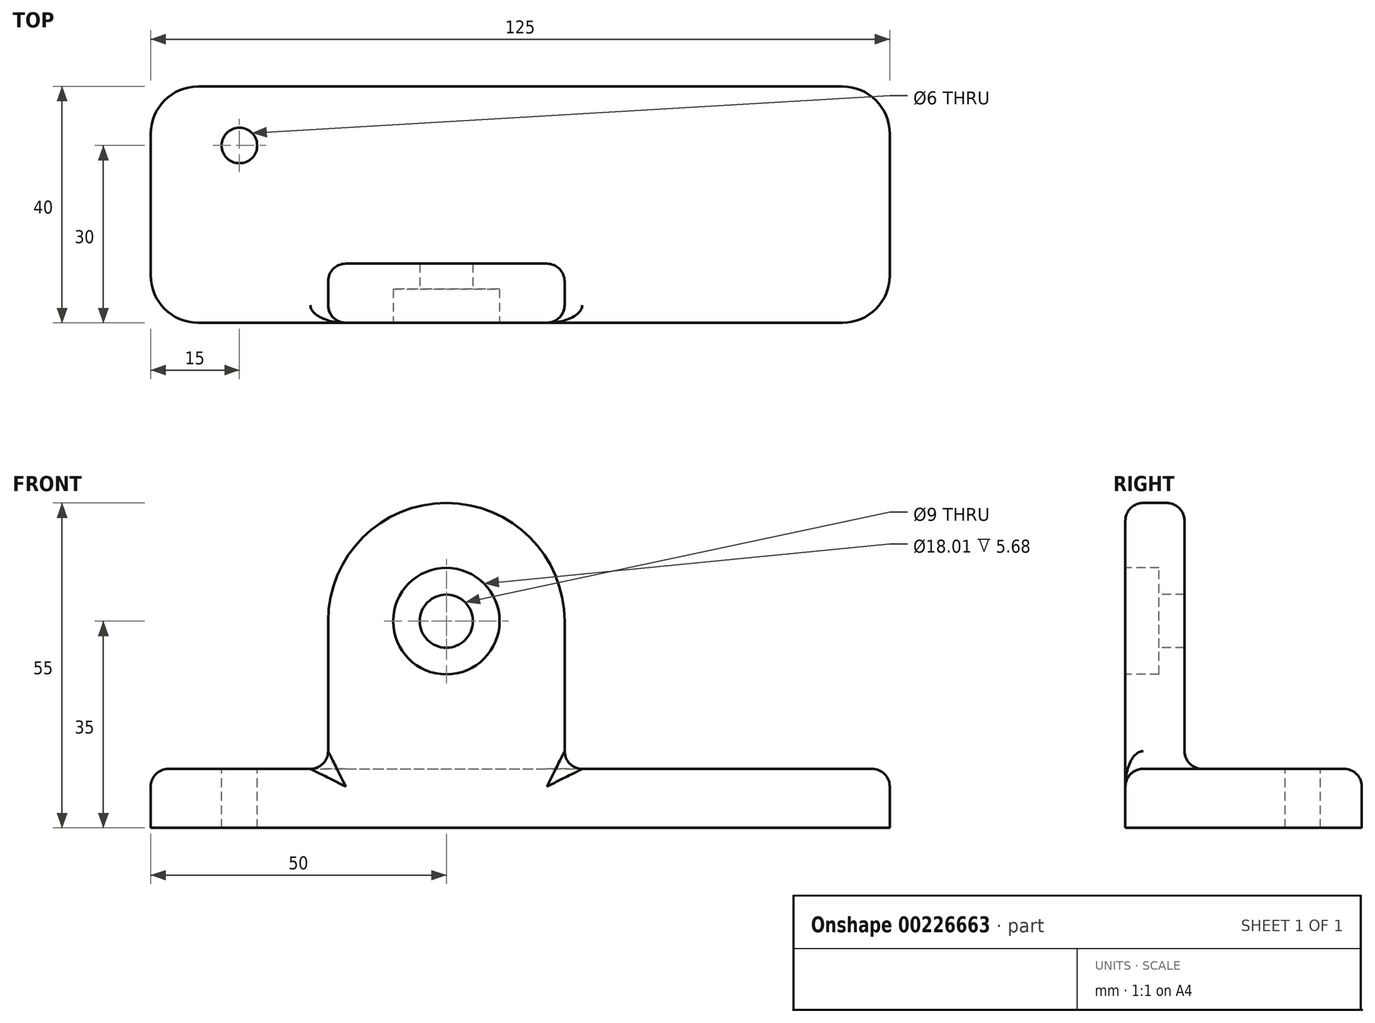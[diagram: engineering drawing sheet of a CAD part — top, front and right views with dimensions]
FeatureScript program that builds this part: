
annotation { "Feature Type Name" : "Feature", "Feature Type Description" : "" }
export const myFeature = defineFeature(function(context is Context, id is Id, definition is map)
    precondition{}
    {
        {
            var Q0;
            Q0=qCreatedBy(makeId("Top.planeOp"),FACE);
            var sketch = newSketch(context, id + "F0", { "sketchPlane" : qUnion([Q0])});
            skLineSegment(sketch, "E0.bottom", {"start": v(-62.5, 20) * mm, "end": v(62.5, 20) * mm});
            skLineSegment(sketch, "E0.top", {"start": v(-62.5, -20) * mm, "end": v(62.5, -20) * mm});
            skLineSegment(sketch, "E0.left", {"start": v(-62.5, 20) * mm, "end": v(-62.5, -20) * mm});
            skLineSegment(sketch, "E0.right", {"start": v(62.5, 20) * mm, "end": v(62.5, -20) * mm});
            skPoint(sketch, "E0.middle", {"position": v(0, 0) * mm});
            skSolve(sketch);
        }
        {
            var Q0;
            Q0 = qSketchRegion(id + "F0", true);
            extrude(context, id + "F1", {"entities" : qUnion([Q0]), "depth" : 10 * mm});
        }
        {
            var Q0;
            Q0=makeQuery(id+"F1.opExtrude","CAP_FACE",FACE,{"disambiguationData":[OSD([sQuery(id+"F0.wireOp",EDGE,"E0.bottom"),sQuery(id+"F0.wireOp",EDGE,"E0.top"),sQuery(id+"F0.wireOp",EDGE,"E0.left"),sQuery(id+"F0.wireOp",EDGE,"E0.right")])],"isStart":false});
            var sketch = newSketch(context, id + "F2", { "sketchPlane" : qUnion([Q0])});
            skLineSegment(sketch, "E1.bottom", {"start": v(-32.5, -20) * mm, "end": v(7.5, -20) * mm});
            skLineSegment(sketch, "E1.top", {"start": v(-32.5, -10) * mm, "end": v(7.5, -10) * mm});
            skLineSegment(sketch, "E1.left", {"start": v(-32.5, -20) * mm, "end": v(-32.5, -10) * mm});
            skLineSegment(sketch, "E1.right", {"start": v(7.5, -20) * mm, "end": v(7.5, -10) * mm});
            skSolve(sketch);
        }
        {
            var Q0;
            Q0 = qSketchRegion(id + "F2", true);
            extrude(context, id + "F3", {"entities" : qUnion([Q0]), "operationType" : NewBodyOperationType.ADD, "depth" : 25 * mm});
        }
        {
            var Q0;
            Q0=makeQuery(id+"F3.boolean.opBoolean","MERGE",FACE,{"derivedFrom":[makeQuery(id+"F1.opExtrude","SWEPT_FACE",FACE,{"disambiguationData":[OSD([sQuery(id+"F0.wireOp",EDGE,"E0.top")])]}),makeQuery(id+"F3.opExtrude","SWEPT_FACE",FACE,{"disambiguationData":[OSD([sQuery(id+"F2.wireOp",EDGE,"E1.bottom")])]})]});
            var sketch = newSketch(context, id + "F4", { "sketchPlane" : qUnion([Q0])});
            skCircle(sketch, "E2", {"center": v(-12.5, 35) * mm, "radius": 20 * mm});
            skSolve(sketch);
        }
        {
            var Q0;
            Q0 = qSketchRegion(id + "F4", true);
            extrude(context, id + "F5", {"entities" : qUnion([Q0]), "operationType" : NewBodyOperationType.ADD, "oppositeDirection" : true, "depth" : 10 * mm});
        }
        {
            var Q0;
            Q0=makeQuery(id+"F1.opExtrude","CAP_FACE",FACE,{"disambiguationData":[OSD([sQuery(id+"F0.wireOp",EDGE,"E0.bottom"),sQuery(id+"F0.wireOp",EDGE,"E0.top"),sQuery(id+"F0.wireOp",EDGE,"E0.left"),sQuery(id+"F0.wireOp",EDGE,"E0.right")])],"isStart":false});
            var sketch = newSketch(context, id + "F6", { "sketchPlane" : qUnion([Q0])});
            skCircle(sketch, "E3", {"center": v(-47.5, 10) * mm, "radius": 3 * mm});
            skSolve(sketch);
        }
        {
            var Q0;
            Q0=makeQuery(id+"F5.boolean.opBoolean","MERGE",FACE,{"derivedFrom":[makeQuery(id+"F3.boolean.opBoolean","MERGE",FACE,{"derivedFrom":[makeQuery(id+"F1.opExtrude","SWEPT_FACE",FACE,{"disambiguationData":[OSD([sQuery(id+"F0.wireOp",EDGE,"E0.top")])]}),makeQuery(id+"F3.opExtrude","SWEPT_FACE",FACE,{"disambiguationData":[OSD([sQuery(id+"F2.wireOp",EDGE,"E1.bottom")])]})]}),makeQuery(id+"F5.opExtrude","CAP_FACE",FACE,{"disambiguationData":[OSD([sQuery(id+"F4.wireOp",EDGE,"E2")])],"isStart":true})]});
            var sketch = newSketch(context, id + "F7", { "sketchPlane" : qUnion([Q0])});
            skCircle(sketch, "E4", {"center": v(-12.5, 35) * mm, "radius": 4.5 * mm});
            skSolve(sketch);
        }
        {
            var Q0;
            Q0 = qSketchRegion(id + "F7", true);
            extrude(context, id + "F8", {"entities" : qUnion([Q0]), "operationType" : NewBodyOperationType.REMOVE, "oppositeDirection" : true, "depth" : 25 * mm});
        }
        {
            var Q0;
            Q0=makeQuery(id+"F5.boolean.opBoolean","MERGE",FACE,{"derivedFrom":[makeQuery(id+"F3.boolean.opBoolean","MERGE",FACE,{"derivedFrom":[makeQuery(id+"F1.opExtrude","SWEPT_FACE",FACE,{"disambiguationData":[OSD([sQuery(id+"F0.wireOp",EDGE,"E0.top")])]}),makeQuery(id+"F3.opExtrude","SWEPT_FACE",FACE,{"disambiguationData":[OSD([sQuery(id+"F2.wireOp",EDGE,"E1.bottom")])]})]}),makeQuery(id+"F5.opExtrude","CAP_FACE",FACE,{"disambiguationData":[OSD([sQuery(id+"F4.wireOp",EDGE,"E2")])],"isStart":true})]});
            var sketch = newSketch(context, id + "F9", { "sketchPlane" : qUnion([Q0])});
            skCircle(sketch, "E5", {"center": v(-12.5, 35) * mm, "radius": 9 * mm});
            skSolve(sketch);
        }
        {
            var Q0;
            Q0 = qSketchRegion(id + "F9", true);
            extrude(context, id + "F10", {"entities" : qUnion([Q0]), "operationType" : NewBodyOperationType.REMOVE, "oppositeDirection" : true, "depth" : 5.68 * mm});
        }
        {
            var Q0;
            Q0=makeQuery(id+"F1.opExtrude","SWEPT_EDGE",EDGE,{"disambiguationData":[OSD([sQuery(id+"F0.wireOp",EDGE,"E0.top"),sQuery(id+"F0.wireOp",EDGE,"E0.right")])]});
            var Q1;
            Q1=makeQuery(id+"F1.opExtrude","SWEPT_EDGE",EDGE,{"disambiguationData":[OSD([sQuery(id+"F0.wireOp",EDGE,"E0.bottom"),sQuery(id+"F0.wireOp",EDGE,"E0.right")])]});
            var Q2;
            Q2=makeQuery(id+"F1.opExtrude","SWEPT_EDGE",EDGE,{"disambiguationData":[OSD([sQuery(id+"F0.wireOp",EDGE,"E0.top"),sQuery(id+"F0.wireOp",EDGE,"E0.left")])]});
            var Q3;
            Q3=makeQuery(id+"F1.opExtrude","SWEPT_EDGE",EDGE,{"disambiguationData":[OSD([sQuery(id+"F0.wireOp",EDGE,"E0.bottom"),sQuery(id+"F0.wireOp",EDGE,"E0.left")])]});
            fillet(context, id + "F11", {"entities" : qUnion([Q0, Q1, Q2, Q3]), "radius" : 8 * mm, "tangentPropagation" : true, "allowEdgeOverflow" : false});
        }
        {
            var Q0;
            {var subQ0=sQuery(id+"F0.wireOp",EDGE,"E0.right");var subQ1=sQuery(id+"F0.wireOp",EDGE,"E0.top");Q0=makeQuery(id+"F3.boolean.opBoolean","SPLIT",EDGE,{"disambiguationData":[TD([makeQuery(id+"F1.opExtrude","SWEPT_FACE",FACE,{"disambiguationData":[OSD([subQ0])]})])],"derivedFrom":makeQuery(id+"F1.opExtrude","CAP_EDGE",EDGE,{"disambiguationData":[OSD([subQ1])],"isStart":false})});}
            var Q1;
            Q1=makeQuery(id+"F3.opExtrude","SWEPT_EDGE",EDGE,{"disambiguationData":[OSD([sQuery(id+"F0.wireOp",EDGE,"E0.top"),sQuery(id+"F2.wireOp",EDGE,"E1.bottom"),sQuery(id+"F2.wireOp",EDGE,"E1.right")])]});
            var Q2;
            Q2=makeQuery(id+"F3.opExtrude","SWEPT_EDGE",EDGE,{"disambiguationData":[OSD([sQuery(id+"F2.wireOp",EDGE,"E1.top"),sQuery(id+"F2.wireOp",EDGE,"E1.right")])]});
            fillet(context, id + "F12", {"entities" : qUnion([Q0, Q1, Q2]), "radius" : 3 * mm, "tangentPropagation" : true, "allowEdgeOverflow" : false});
        }
        {
            var Q0;
            Q0=makeQuery(id+"F6.imprint","IMPRINT",FACE,{"disambiguationData":[TD([[makeQuery(id+"F6.imprint","IMPRINT",EDGE,{"derivedFrom":sQuery(id+"F6.wireOp",EDGE,"E3")}),1.0]])]});
            extrude(context, id + "F13", {"entities" : qUnion([Q0]), "operationType" : NewBodyOperationType.REMOVE, "oppositeDirection" : true, "depth" : 25 * mm});
        }
        {
            var Q0;
            {var subQ0=sQuery(id+"F2.wireOp",EDGE,"E1.bottom");var subQ1=sQuery(id+"F0.wireOp",EDGE,"E0.right");var subQ2=sQuery(id+"F0.wireOp",EDGE,"E0.top");var subQ3=sQuery(id+"F2.wireOp",EDGE,"E1.right");Q0=makeQuery(id+"F12.opFillet","BLEND_EDGE",EDGE,{"blendedFrom":[makeQuery(id+"F3.opExtrude","SWEPT_EDGE",EDGE,{"disambiguationData":[OSD([subQ2,subQ0,subQ3])]}),makeQuery(id+"F3.boolean.opBoolean","SPLIT",EDGE,{"disambiguationData":[TD([makeQuery(id+"F1.opExtrude","SWEPT_FACE",FACE,{"disambiguationData":[OSD([subQ1])]})])],"derivedFrom":makeQuery(id+"F1.opExtrude","CAP_EDGE",EDGE,{"disambiguationData":[OSD([subQ2])],"isStart":false})})],"blendedInto":[]});}
            fillet(context, id + "F14", {"entities" : qUnion([Q0]), "radius" : 3 * mm, "tangentPropagation" : true, "allowEdgeOverflow" : false});
        }
    });
